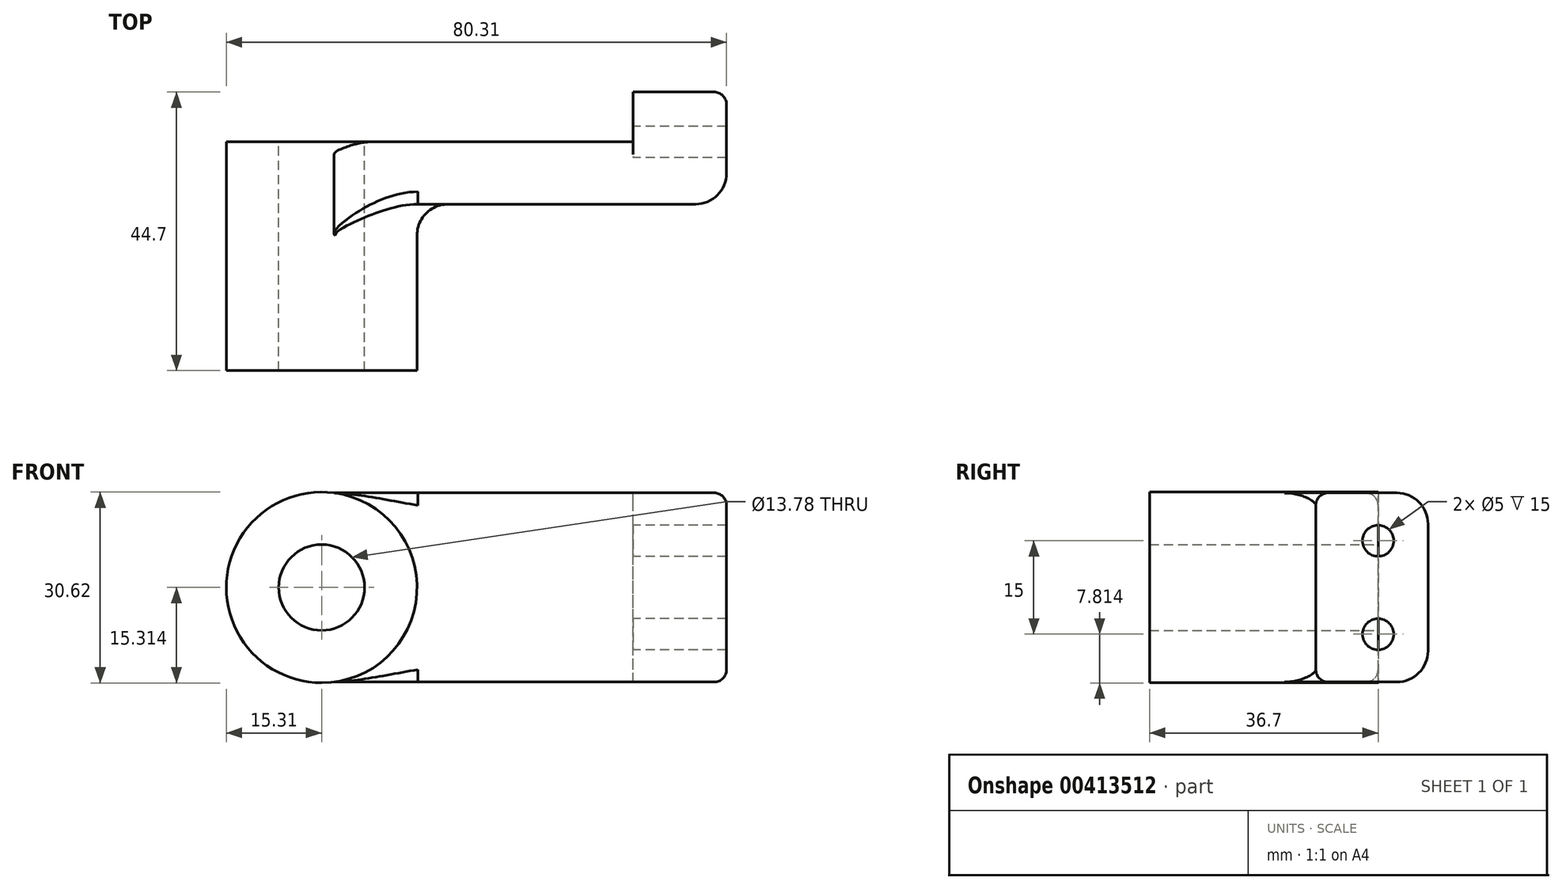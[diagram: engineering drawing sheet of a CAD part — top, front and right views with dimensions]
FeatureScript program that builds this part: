
annotation { "Feature Type Name" : "Feature", "Feature Type Description" : "" }
export const myFeature = defineFeature(function(context is Context, id is Id, definition is map)
    precondition{}
    {
        {
            var Q0;
            Q0=qCreatedBy(makeId("Front.planeOp"),FACE);
            var sketch = newSketch(context, id + "F0", { "sketchPlane" : qUnion([Q0])});
            skLineSegment(sketch, "E0.bottom", {"start": v(0, 0) * mm, "end": v(-50, 0) * mm});
            skLineSegment(sketch, "E0.top", {"start": v(0, 30.37) * mm, "end": v(-50, 30.37) * mm});
            skLineSegment(sketch, "E0.left", {"start": v(0, 0) * mm, "end": v(0, 30.37) * mm});
            skLineSegment(sketch, "E0.right", {"start": v(-50, 0) * mm, "end": v(-50, 30.37) * mm});
            skCircle(sketch, "E1", {"center": v(-50, 15.18) * mm, "radius": 15.31 * mm});
            skCircle(sketch, "E2", {"center": v(-50, 15.18) * mm, "radius": 6.9 * mm});
            skSolve(sketch);
        }
        {
            var Q0;
            Q0 = qSketchRegion(id + "F0", true);
            extrude(context, id + "F1", {"entities" : qUnion([Q0]), "depth" : 10 * mm});
        }
        {
            var Q0;
            {var subQ0=sQuery(id+"F0.wireOp",EDGE,"E0.right");var subQ5=sQuery(id+"F0.wireOp",EDGE,"E0.bottom");var subQ6=makeQuery(id+"F0.imprint","INTERSECT",VERTEX,{"derivedFrom":[subQ5,subQ0]});Q0=makeQuery(id+"F0.imprint","IMPRINT",FACE,{"disambiguationData":[TD([[makeQuery(id+"F0.imprint","IMPRINT",EDGE,{"disambiguationData":[TD([[subQ6,1.0]])],"derivedFrom":subQ5}),1.0]])]});}
            var Q1;
            {var subQ0=sQuery(id+"F0.wireOp",EDGE,"E0.right");var subQ5=sQuery(id+"F0.wireOp",EDGE,"E0.bottom");var subQ6=makeQuery(id+"F0.imprint","INTERSECT",VERTEX,{"derivedFrom":[subQ5,subQ0]});Q1=makeQuery(id+"F0.imprint","IMPRINT",FACE,{"disambiguationData":[TD([[makeQuery(id+"F0.imprint","IMPRINT",EDGE,{"disambiguationData":[TD([[subQ6,1.0]])],"derivedFrom":subQ5}),-1.0]])]});}
            extrude(context, id + "F2", {"entities" : qUnion([Q0, Q1]), "operationType" : NewBodyOperationType.ADD, "depth" : 36.7 * mm});
        }
        {
            var Q0;
            Q0=makeQuery(id+"F1.opExtrude","SWEPT_FACE",FACE,{"disambiguationData":[OSD([sQuery(id+"F0.wireOp",EDGE,"E0.left")])]});
            var sketch = newSketch(context, id + "F3", { "sketchPlane" : qUnion([Q0])});
            skLineSegment(sketch, "E3.bottom", {"start": v(-10, 0) * mm, "end": v(8, 0) * mm});
            skLineSegment(sketch, "E3.top", {"start": v(-10, 30.37) * mm, "end": v(8, 30.37) * mm});
            skLineSegment(sketch, "E3.left", {"start": v(-10, 0) * mm, "end": v(-10, 30.37) * mm});
            skLineSegment(sketch, "E3.right", {"start": v(8, 0) * mm, "end": v(8, 30.37) * mm});
            skLineSegment(sketch, "E4", {"start": v(-10, 15.18) * mm, "end": v(8, 15.18) * mm});
            skCircle(sketch, "E5", {"center": v(0, 7.68) * mm, "radius": 2.5 * mm});
            skCircle(sketch, "E6.MirrorC", {"center": v(0, 22.68) * mm, "radius": 2.5 * mm});
            skSolve(sketch);
        }
        {
            var Q0;
            Q0 = qSketchRegion(id + "F3", true);
            extrude(context, id + "F4", {"entities" : qUnion([Q0]), "operationType" : NewBodyOperationType.ADD, "depth" : 15 * mm});
        }
        {
            var Q0;
            {var subQ0=sQuery(id+"F0.wireOp",EDGE,"E1");Q0=makeQuery(id+"F2.boolean.opBoolean","INTERSECT",EDGE,{"derivedFrom":[makeQuery(id+"F1.opExtrude","CAP_FACE",FACE,{"disambiguationData":[OSD([sQuery(id+"F0.wireOp",EDGE,"E0.bottom"),sQuery(id+"F0.wireOp",EDGE,"E0.top"),sQuery(id+"F0.wireOp",EDGE,"E0.left"),subQ0,sQuery(id+"F0.wireOp",EDGE,"E2")])],"isStart":false}),makeQuery(id+"F2.opExtrude","SWEPT_FACE",FACE,{"disambiguationData":[OSD([subQ0])]})]});}
            var Q1;
            Q1=makeQuery(id+"F4.opExtrude","CAP_EDGE",EDGE,{"disambiguationData":[OSD([sQuery(id+"F3.wireOp",EDGE,"E3.left")])],"isStart":false});
            var Q2;
            Q2=makeQuery(id+"F4.opExtrude","SWEPT_EDGE",EDGE,{"disambiguationData":[OSD([sQuery(id+"F3.wireOp",EDGE,"E3.top"),sQuery(id+"F3.wireOp",EDGE,"E3.right")])]});
            var Q3;
            Q3=makeQuery(id+"F4.opExtrude","SWEPT_EDGE",EDGE,{"disambiguationData":[OSD([sQuery(id+"F3.wireOp",EDGE,"E3.bottom"),sQuery(id+"F3.wireOp",EDGE,"E3.right")])]});
            fillet(context, id + "F5", {"entities" : qUnion([Q0, Q1, Q2, Q3]), "radius" : 5 * mm, "tangentPropagation" : true, "allowEdgeOverflow" : false});
        }
        {
            var Q0;
            Q0=makeQuery(id+"F4.boolean.opBoolean","MERGE",EDGE,{"derivedFrom":[makeQuery(id+"F1.opExtrude","CAP_EDGE",EDGE,{"disambiguationData":[OSD([sQuery(id+"F0.wireOp",EDGE,"E0.top")])],"isStart":false}),makeQuery(id+"F4.opExtrude","SWEPT_EDGE",EDGE,{"disambiguationData":[OSD([sQuery(id+"F3.wireOp",EDGE,"E3.top"),sQuery(id+"F3.wireOp",EDGE,"E3.left")])]})]});
            var Q1;
            Q1=makeQuery(id+"F1.opExtrude","CAP_EDGE",EDGE,{"disambiguationData":[OSD([sQuery(id+"F0.wireOp",EDGE,"E0.top")])],"isStart":true});
            var Q2;
            Q2=makeQuery(id+"F1.opExtrude","CAP_EDGE",EDGE,{"disambiguationData":[OSD([sQuery(id+"F0.wireOp",EDGE,"E0.bottom")])],"isStart":true});
            fillet(context, id + "F6", {"entities" : qUnion([Q0, Q1, Q2]), "radius" : 2 * mm, "tangentPropagation" : true, "allowEdgeOverflow" : false});
        }
    });
